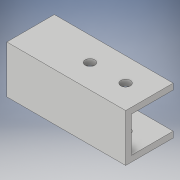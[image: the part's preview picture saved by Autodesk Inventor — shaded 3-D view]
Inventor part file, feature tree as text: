
AUTODESK INVENTOR PART (.ipt)
format: ipt  version: 2018 (Build 220112000, 112)  size: 116,224 bytes
history: native  units: in
note: dims shown in document units (in); Inventor stores cm internally (conversion verified against a paired STEP export)
features: sketch x4, other x3
ambient origin geometry x8: Origin, YZ Plane, XZ Plane, XY Plane, X Axis, Y Axis, Z Axis, Center Point
bodies: Solid1 (feature_tree)
feature tree (7):
  other  "wheel tip connector 1_MIR.ipt"
  other  "Solid1::wheel tip connector 1_MIR.ipt"
  other  "TaggingFeature1"
  sketch  "Sketch1"  dims[d0=0.3937in]
  sketch  "Sketch2"
  sketch  "Sketch3"
  sketch  "Sketch4"
